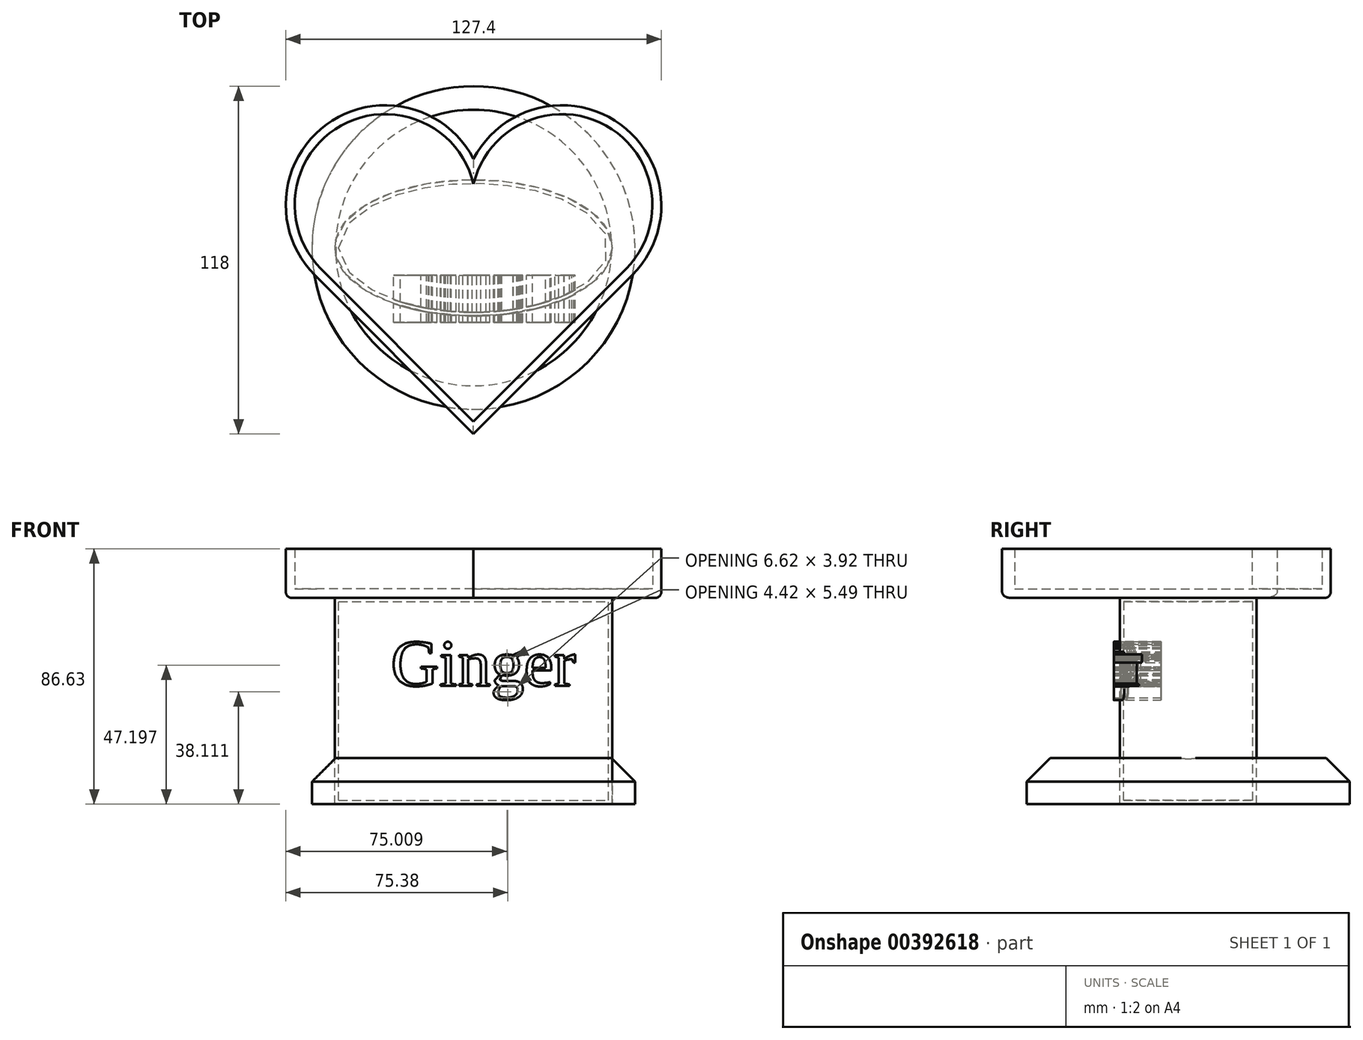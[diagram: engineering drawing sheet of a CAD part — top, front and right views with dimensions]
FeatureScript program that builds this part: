
annotation { "Feature Type Name" : "Feature", "Feature Type Description" : "" }
export const myFeature = defineFeature(function(context is Context, id is Id, definition is map)
    precondition{}
    {
        {
            var Q0;
            Q0=qCreatedBy(makeId("Top.planeOp"),FACE);
            var sketch = newSketch(context, id + "F0", { "sketchPlane" : qUnion([Q0])});
            skLineSegment(sketch, "E0", {"start": v(0, -53.9) * mm, "end": v(53.83, 0) * mm});
            skArc(sketch, "E1", {"start": v(53.83, 0) * mm, "mid": v(49.9, 51.09) * mm, "end": v(0, 39.44) * mm});
            skLineSegment(sketch, "E2", {"start": v(0, -53.9) * mm, "end": v(-53.83, 0) * mm});
            skArc(sketch, "E3", {"start": v(-53.83, 0) * mm, "mid": v(-49.9, 51.09) * mm, "end": v(0, 39.44) * mm});
            skSolve(sketch);
        }
        {
            var Q0;
            Q0=makeQuery(id+"F0.imprint","IMPRINT",FACE,{"disambiguationData":[TD([[makeQuery(id+"F0.imprint","IMPRINT",EDGE,{"derivedFrom":sQuery(id+"F0.wireOp",EDGE,"E0")}),1.0]])]});
            extrude(context, id + "F1", {"entities" : qUnion([Q0]), "depth" : 16.63 * mm});
        }
        {
            var Q0;
            Q0=makeQuery(id+"F1.opExtrude","CAP_FACE",FACE,{"disambiguationData":[OSD([sQuery(id+"F0.wireOp",EDGE,"E0"),sQuery(id+"F0.wireOp",EDGE,"E1"),sQuery(id+"F0.wireOp",EDGE,"E2"),sQuery(id+"F0.wireOp",EDGE,"E3")])],"isStart":true});
            var sketch = newSketch(context, id + "F2", { "sketchPlane" : qUnion([Q0])});
            skSolve(sketch);
        }
        {
            var Q0;
            Q0=makeQuery(id+"F1.opExtrude","CAP_FACE",FACE,{"disambiguationData":[OSD([sQuery(id+"F0.wireOp",EDGE,"E0"),sQuery(id+"F0.wireOp",EDGE,"E1"),sQuery(id+"F0.wireOp",EDGE,"E2"),sQuery(id+"F0.wireOp",EDGE,"E3")])],"isStart":false});
            extrude(context, id + "F3", {"entities" : qUnion([Q0]), "operationType" : NewBodyOperationType.ADD, "oppositeDirection" : true, "depth" : 6.3 * mm});
        }
        {
            var Q0;
            Q0=makeQuery(id+"F1.opExtrude","CAP_FACE",FACE,{"disambiguationData":[OSD([sQuery(id+"F0.wireOp",EDGE,"E0"),sQuery(id+"F0.wireOp",EDGE,"E1"),sQuery(id+"F0.wireOp",EDGE,"E2"),sQuery(id+"F0.wireOp",EDGE,"E3")])],"isStart":false});
            shell(context, id + "F4", {"entities" : qUnion([Q0]), "thickness" : 3 * mm});
        }
        {
            var Q0;
            Q0=makeQuery(id+"F1.opExtrude","CAP_EDGE",EDGE,{"disambiguationData":[OSD([sQuery(id+"F0.wireOp",EDGE,"E1")])],"isStart":true});
            var Q1;
            Q1=makeQuery(id+"F1.opExtrude","CAP_EDGE",EDGE,{"disambiguationData":[OSD([sQuery(id+"F0.wireOp",EDGE,"E0")])],"isStart":true});
            var Q2;
            Q2=makeQuery(id+"F1.opExtrude","CAP_EDGE",EDGE,{"disambiguationData":[OSD([sQuery(id+"F0.wireOp",EDGE,"E3")])],"isStart":true});
            var Q3;
            Q3=makeQuery(id+"F1.opExtrude","CAP_EDGE",EDGE,{"disambiguationData":[OSD([sQuery(id+"F0.wireOp",EDGE,"E2")])],"isStart":true});
            fillet(context, id + "F5", {"entities" : qUnion([Q0, Q1, Q2, Q3]), "radius" : 2 * mm, "tangentPropagation" : true, "allowEdgeOverflow" : false});
        }
        {
            var Q0;
            Q0=makeQuery(id+"F2.imprint","IMPRINT",FACE,{"disambiguationData":[TD([[makeQuery(id+"F2.imprint","IMPRINT",EDGE,{"derivedFrom":makeQuery(id+"F1.opExtrude","CAP_EDGE",EDGE,{"disambiguationData":[OSD([sQuery(id+"F0.wireOp",EDGE,"E0")])],"isStart":true})}),-1.0]])]});
            var sketch = newSketch(context, id + "F6", { "sketchPlane" : qUnion([Q0])});
            skEllipse(sketch, "E4", {"center": v(0, -9.28) * mm, "majorRadius": 47.02 * mm, "minorRadius": 23.15 * mm, "majorAxis": v(1, 0)});
            skSolve(sketch);
        }
        {
            var Q0;
            Q0=makeQuery(id+"F6.imprint","IMPRINT",FACE,{"disambiguationData":[TD([[makeQuery(id+"F6.imprint","IMPRINT",EDGE,{"derivedFrom":sQuery(id+"F6.wireOp",EDGE,"E4")}),1.0]])]});
            var Q1;
            Q1=sQuery(id+"F6.wireOp",EDGE,"E4");
            extrude(context, id + "F7", {"entities" : qUnion([Q0]), "surfaceEntities" : qUnion([Q1]), "depth" : 70 * mm});
        }
        {
            var Q0;
            Q0=makeQuery(id+"F7.opExtrude","CAP_FACE",FACE,{"disambiguationData":[OSD([sQuery(id+"F6.wireOp",EDGE,"E4")])],"isStart":false});
            var Q1;
            Q1=makeQuery(id+"F7.opExtrude","SWEPT_BODY",BODY,{"disambiguationData":[OSD([sQuery(id+"F6.wireOp",EDGE,"E4")])]});
            shell(context, id + "F8", {"isHollow" : true, "entities" : qUnion([Q0]), "parts" : qUnion([Q1]), "thickness" : 1.25 * mm});
        }
        {
            var Q0;
            Q0=makeQuery(id+"F7.opExtrude","CAP_FACE",FACE,{"disambiguationData":[OSD([sQuery(id+"F6.wireOp",EDGE,"E4")])],"isStart":false});
            var sketch = newSketch(context, id + "F9", { "sketchPlane" : qUnion([Q0])});
            skCircle(sketch, "E5", {"center": v(0, -9.28) * mm, "radius": 54.83 * mm});
            skSolve(sketch);
        }
        {
            var Q0;
            Q0=makeQuery(id+"F9.imprint","IMPRINT",FACE,{"disambiguationData":[TD([[makeQuery(id+"F9.imprint","IMPRINT",EDGE,{"derivedFrom":sQuery(id+"F9.wireOp",EDGE,"E5")}),1.0]])]});
            var Q1;
            Q1=sQuery(id+"F9.wireOp",EDGE,"E5");
            extrude(context, id + "F10", {"entities" : qUnion([Q0]), "surfaceEntities" : qUnion([Q1]), "oppositeDirection" : true, "depth" : 15.6 * mm});
        }
        {
            var Q0;
            Q0=makeQuery(id+"F10.opExtrude","CAP_EDGE",EDGE,{"disambiguationData":[OSD([sQuery(id+"F9.wireOp",EDGE,"E5")])],"isStart":false});
            chamfer(context, id + "F11", {"entities" : qUnion([Q0]), "width" : 8 * mm, "tangentPropagation" : true});
        }
        {
            var Q0;
            Q0=qCreatedBy(makeId("Front.planeOp"),FACE);
            var sketch = newSketch(context, id + "F12", { "sketchPlane" : qUnion([Q0])});
            skText(sketch, "E6", { "text": "Ginger", "fontName": "Tinos-Regular.ttf"});
            const initialGuessF12  = {"E6": [-0.02803, -0.02986, 1, 0, 0.01626]};
            skSetInitialGuess(sketch, initialGuessF12);
            skSolve(sketch);
        }
        {
            var Q0;
            Q0 = qSketchRegion(id + "F12", true);
            extrude(context, id + "F13", {"entities" : qUnion([Q0]), "operationType" : NewBodyOperationType.ADD, "depth" : 16 * mm});
        }
        {
            var Q0;
            Q0=qCreatedBy(makeId("Front.planeOp"),FACE);
            cPlane(context, id + "F14", {"entities" : qUnion([Q0]), "cplaneType" : CPlaneType.OFFSET, "offset" : 10 * mm, "width" : 150 * mm, "height" : 150 * mm});
        }
        {
            var Q0;
            Q0=qCreatedBy(id+"F14.planeOp",FACE);
            var sketch = newSketch(context, id + "F15", { "sketchPlane" : qUnion([Q0])});
            skLineSegment(sketch, "E7", {"start": v(-41.42, -20.02) * mm, "end": v(-27.54, -20.02) * mm});
            skCircle(sketch, "E8", {"center": v(-35.17, -13) * mm, "radius": 2.5 * mm});
            skSolve(sketch);
        }
        {
            var Q0;
            Q0=sQuery(id+"F15.wireOp",EDGE,"E8");
            var Q1;
            Q1=sQuery(id+"F15.wireOp",EDGE,"E7");
            revolve(context, id + "F16", {"bodyType" : ToolBodyType.SURFACE, "surfaceEntities" : qUnion([Q0]), "axis" : qUnion([Q1]), "revolveType" : RevolveType.FULL});
        }
    });
